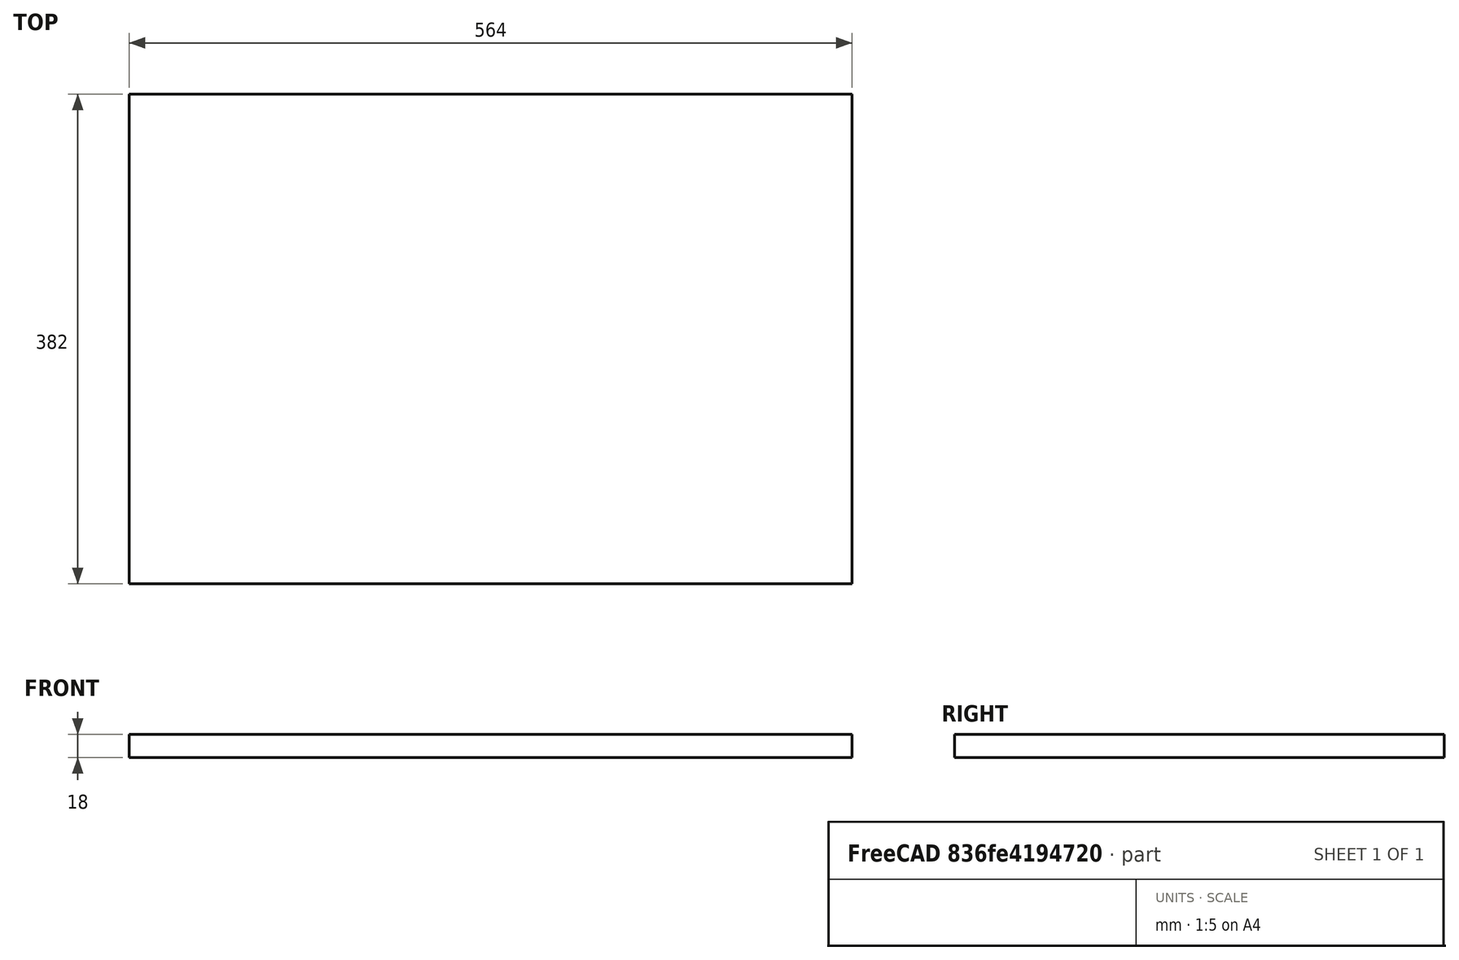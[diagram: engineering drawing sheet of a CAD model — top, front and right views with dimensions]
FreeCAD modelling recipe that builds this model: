
FCSTD DOCUMENT  (FreeCAD 0.18R4 (GitTag))
Label: shelf
License: All rights reserved
LicenseURL: http://en.wikipedia.org/wiki/All_rights_reserved
objects: Sketcher::SketchObject×1, PartDesign::Pad×1, PartDesign::Body×1
note: 4 computed .brp shape members not serialized (recipe doc carries the construction recipe); baked Part::Feature solids carry a one-line shape summary decoded from their .brp

FEATURE [Sketcher::SketchObject] Sketch
  MapMode = 5
  Support = -> [XY_Plane]
  sketch-geometry (4):
    g0: LineSegment StartX=0 StartY=0 StartZ=0 EndX=-564 EndY=0 EndZ=0
    g1: LineSegment StartX=-564 StartY=0 StartZ=0 EndX=-564 EndY=382 EndZ=0
    g2: LineSegment StartX=-564 StartY=382 StartZ=0 EndX=0 EndY=382 EndZ=0
    g3: LineSegment StartX=0 StartY=382 StartZ=0 EndX=0 EndY=0 EndZ=0
  constraints (11):
    c: Coincident(g0,g1)
    c: Coincident(g1,g2)
    c: Coincident(g2,g3)
    c: Coincident(g3,g0)
    c: Horizontal(g0)
    c: Horizontal(g2)
    c: Vertical(g1)
    c: Vertical(g3)
    c: Coincident(g0,g-1)
    c: DistanceX(g0,g0) = 564
    c: DistanceY(g3,g3) = 382
FEATURE [PartDesign::Pad] Pad
  Length = 18
  Length2 = 100
  Profile = -> Sketch
  Type = 0
FEATURE [PartDesign::Body] Body
  Group = -> [Sketch,Pad]
  Origin = -> Origin
  Tip = -> Pad
